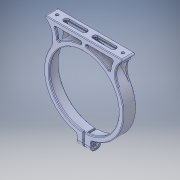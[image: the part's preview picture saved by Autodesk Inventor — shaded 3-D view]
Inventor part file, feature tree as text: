
AUTODESK INVENTOR PART (.ipt)
format: ipt  version: 2016 (Build 200138000, 138)  size: 504,320 bytes
history: native  units: in
note: dims shown in document units (in); Inventor stores cm internally (conversion verified against a paired STEP export)
features: fillet x1
ambient origin geometry x8: Origin, YZ Plane, XZ Plane, XY Plane, X Axis, Y Axis, Z Axis, Center Point
bodies: Solid1 (feature_tree)
feature tree (1):
  fillet  "Fillet5"  [1 undecoded]
note: 1 required parameter value undecoded (feature->parameter linkage not recoverable at this tier; creation-order binding heuristic only, values carry confidence <= 0.55)
